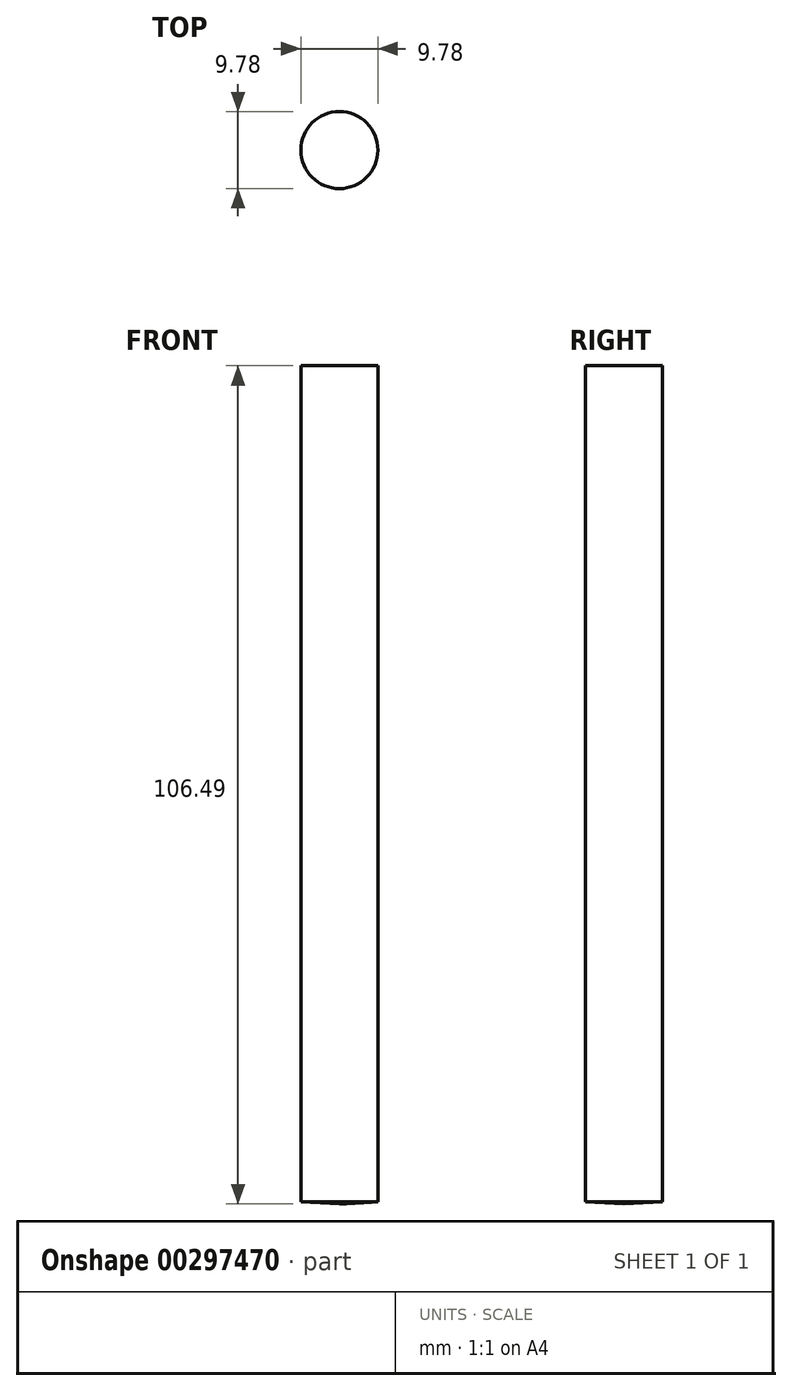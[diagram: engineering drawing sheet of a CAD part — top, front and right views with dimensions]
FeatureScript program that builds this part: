
annotation { "Feature Type Name" : "Feature", "Feature Type Description" : "" }
export const myFeature = defineFeature(function(context is Context, id is Id, definition is map)
    precondition{}
    {
        {
            var Q0;
            Q0=qCreatedBy(makeId("Front.planeOp"),FACE);
            var sketch = newSketch(context, id + "F0", { "sketchPlane" : qUnion([Q0])});
            skLineSegment(sketch, "E0", {"start": v(-35.54, 67.35) * mm, "end": v(-35.54, -38.85) * mm});
            skLineSegment(sketch, "E1", {"start": v(-35.54, 67.35) * mm, "end": v(-30.65, 67.35) * mm});
            skLineSegment(sketch, "E2", {"start": v(-30.65, 67.35) * mm, "end": v(-30.65, -39.14) * mm});
            skLineSegment(sketch, "E3", {"start": v(-30.65, -39.14) * mm, "end": v(-35.54, -38.85) * mm});
            skSolve(sketch);
        }
        {
            var Q0;
            Q0=makeQuery(id+"F0.imprint","IMPRINT",FACE,{"disambiguationData":[TD([[makeQuery(id+"F0.imprint","IMPRINT",EDGE,{"derivedFrom":sQuery(id+"F0.wireOp",EDGE,"E0")}),1.0]])]});
            var Q1;
            Q1=sQuery(id+"F0.wireOp",EDGE,"E2");
            revolve(context, id + "F1", {"entities" : qUnion([Q0]), "axis" : qUnion([Q1]), "revolveType" : RevolveType.FULL});
        }
    });
